annotation { "Feature Type Name" : "Feature", "Feature Type Description" : "" }
export const myFeature = defineFeature(function(context is Context, id is Id, definition is map)
    precondition{}
    {
        {
            var Q0;
            Q0=qCreatedBy(makeId("Right.planeOp"),FACE);
            var sketch = newSketch(context, id + "F0", { "sketchPlane" : qUnion([Q0])});
            skFitSpline(sketch, "E0", {"points": [v(-57.8, 46.93) * mm, v(-52.74, 44.85) * mm, v(-66.15, 19.52) * mm], "startDerivative": vector(22.12, -2.36) * mm, "endDerivative": vector(-31.77, -46.68) * mm});
            skFitSpline(sketch, "E1", {"points": [v(-66.15, 19.52) * mm, v(-70.33, 23.7) * mm], "startDerivative": vector(-4.17, 4.17) * mm, "endDerivative": vector(-4.17, 4.17) * mm});
            skFitSpline(sketch, "E2", {"points": [v(-70.33, 23.7) * mm, v(-55.57, 46.7) * mm], "startDerivative": vector(14.76, 23) * mm, "endDerivative": vector(14.76, 23) * mm});
            skSolve(sketch);
        }
        {
            var Q0;
            Q0=qCreatedBy(makeId("Right.planeOp"),FACE);
            var sketch = newSketch(context, id + "F1", { "sketchPlane" : qUnion([Q0])});
            skFitSpline(sketch, "E3", {"points": [v(-47.68, 42.46) * mm, v(-44.4, 40.68) * mm, v(-56.32, 17.13) * mm, v(-59.9, 19.52) * mm, v(-47.68, 42.46) * mm]});
            skFitSpline(sketch, "E4", {"points": [v(-39.33, 37.7) * mm, v(-35.16, 34.42) * mm, v(-45.6, 14.15) * mm, v(-49.17, 15.94) * mm, v(-39.33, 37.7) * mm]});
            skSolve(sketch);
        }
        {
            var Q0;
            Q0=qCreatedBy(makeId("Right.planeOp"),FACE);
            var sketch = newSketch(context, id + "F2", { "sketchPlane" : qUnion([Q0])});
            skText(sketch, "E5", { "text": "Adida\'s", "fontName": "OpenSans-Regular.ttf"});
            const initialGuessF2  = {"E5": [-0.0745, 0.00372, 1, 0, 0.00954]};
            skSetInitialGuess(sketch, initialGuessF2);
            skSolve(sketch);
        }
        {
            var Q0;
            Q0=qCreatedBy(makeId("Right.planeOp"),FACE);
            var sketch = newSketch(context, id + "F3", { "sketchPlane" : qUnion([Q0])});
            skFitSpline(sketch, "E6", {"points": [v(-63.77, -27.27) * mm, v(-61.98, -35.9) * mm, v(-13.7, -9.68) * mm, v(-13.11, -9.68) * mm], "startDerivative": vector(-9.49, -47.77) * mm, "endDerivative": vector(3.68, -3.66) * mm});
            skFitSpline(sketch, "E7", {"points": [v(-63.77, -27.27) * mm, v(-59.6, -31.44) * mm, v(-15.8, -7) * mm, v(-13.7, -7) * mm], "startDerivative": vector(8.17, -29.74) * mm, "endDerivative": vector(8.8, -5.9) * mm});
            skSolve(sketch);
        }
        {
            var Q0;
            Q0=qCreatedBy(makeId("Right.planeOp"),FACE);
            var sketch = newSketch(context, id + "F4", { "sketchPlane" : qUnion([Q0])});
            skText(sketch, "E8", { "text": "NIKE", "fontName": "OpenSans-Regular.ttf"});
            const initialGuessF4  = {"E8": [-0.06824, -0.05766, 1, 0, 0.01013]};
            skSetInitialGuess(sketch, initialGuessF4);
            skSolve(sketch);
        }
        {
            var Q0;
            Q0 = qSketchRegion(id + "F4", true);
            extrude(context, id + "F5", {"entities" : qUnion([Q0]), "depth" : 25.4 * mm, "offsetDistance" : 25.4 * mm});
        }
        {
            var Q0;
            Q0 = qSketchRegion(id + "F2", true);
            extrude(context, id + "F6", {"entities" : qUnion([Q0]), "depth" : 25.4 * mm, "offsetDistance" : 25.4 * mm});
        }
        {
            var Q0;
            Q0=qCreatedBy(makeId("Right.planeOp"),FACE);
            var sketch = newSketch(context, id + "F7", { "sketchPlane" : qUnion([Q0])});
            skText(sketch, "E9", { "text": "UNDER ARMOUR", "fontName": "OpenSans-Regular.ttf"});
            const initialGuessF7  = {"E9": [0.00447, 0.00372, 1, 0, 0.00894]};
            skSetInitialGuess(sketch, initialGuessF7);
            skSolve(sketch);
        }
        {
            var Q0;
            Q0 = qSketchRegion(id + "F7", true);
            extrude(context, id + "F8", {"entities" : qUnion([Q0]), "depth" : 25.4 * mm, "offsetDistance" : 25.4 * mm});
        }
        {
            var Q0;
            Q0=makeQuery(id+"F6.opExtrude","CAP_FACE",FACE,{"disambiguationData":[OSD([sQuery(id+"F2.wireOp",EDGE,"E5.sketch_text.stroke-73"),sQuery(id+"F2.wireOp",EDGE,"E5.sketch_text.stroke-74"),sQuery(id+"F2.wireOp",EDGE,"E5.sketch_text.stroke-75"),sQuery(id+"F2.wireOp",EDGE,"E5.sketch_text.stroke-76"),sQuery(id+"F2.wireOp",EDGE,"E5.sketch_text.stroke-77"),sQuery(id+"F2.wireOp",EDGE,"E5.sketch_text.stroke-78"),sQuery(id+"F2.wireOp",EDGE,"E5.sketch_text.stroke-79"),sQuery(id+"F2.wireOp",EDGE,"E5.sketch_text.stroke-80"),sQuery(id+"F2.wireOp",EDGE,"E5.sketch_text.stroke-81"),sQuery(id+"F2.wireOp",EDGE,"E5.sketch_text.stroke-82"),sQuery(id+"F2.wireOp",EDGE,"E5.sketch_text.stroke-83"),sQuery(id+"F2.wireOp",EDGE,"E5.sketch_text.stroke-84"),sQuery(id+"F2.wireOp",EDGE,"E5.sketch_text.stroke-85"),sQuery(id+"F2.wireOp",EDGE,"E5.sketch_text.stroke-86"),sQuery(id+"F2.wireOp",EDGE,"E5.sketch_text.stroke-87"),sQuery(id+"F2.wireOp",EDGE,"E5.sketch_text.stroke-88"),sQuery(id+"F2.wireOp",EDGE,"E5.sketch_text.stroke-89"),sQuery(id+"F2.wireOp",EDGE,"E5.sketch_text.stroke-90"),sQuery(id+"F2.wireOp",EDGE,"E5.sketch_text.stroke-91"),sQuery(id+"F2.wireOp",EDGE,"E5.sketch_text.stroke-92"),sQuery(id+"F2.wireOp",EDGE,"E5.sketch_text.stroke-93"),sQuery(id+"F2.wireOp",EDGE,"E5.sketch_text.stroke-94"),sQuery(id+"F2.wireOp",EDGE,"E5.sketch_text.stroke-95"),sQuery(id+"F2.wireOp",EDGE,"E5.sketch_text.stroke-96"),sQuery(id+"F2.wireOp",EDGE,"E5.sketch_text.stroke-97"),sQuery(id+"F2.wireOp",EDGE,"E5.sketch_text.stroke-98"),sQuery(id+"F2.wireOp",EDGE,"E5.sketch_text.stroke-99")])],"isStart":false});
            var sketch = newSketch(context, id + "F9", { "sketchPlane" : qUnion([Q0])});
            skText(sketch, "E10", { "text": "Reebok\n", "fontName": "OpenSans-Regular.ttf"});
            const initialGuessF9  = {"E10": [0.00547, -0.06362, 1, 0, 0.00954]};
            skSetInitialGuess(sketch, initialGuessF9);
            skSolve(sketch);
        }
        {
            var Q0;
            Q0 = qSketchRegion(id + "F9", true);
            extrude(context, id + "F10", {"entities" : qUnion([Q0]), "depth" : 25.4 * mm, "offsetDistance" : 25.4 * mm});
        }
        {
            var Q0;
            Q0=sQuery(id+"F3.wireOp",EDGE,"E7");
            var Q1;
            Q1=sQuery(id+"F3.wireOp",EDGE,"E6");
            extrude(context, id + "F11", {"bodyType" : ToolBodyType.SURFACE, "surfaceEntities" : qUnion([Q0, Q1]), "depth" : 25.4 * mm, "offsetDistance" : 25.4 * mm});
        }
        {
            var Q0;
            {var subQ0=sQuery(id+"F0.wireOp",EDGE,"E1");Q0=makeQuery(id+"F0.imprint","IMPRINT",FACE,{"disambiguationData":[TD([[makeQuery(id+"F0.imprint","IMPRINT",EDGE,{"derivedFrom":subQ0}),-1.0]])]});}
            extrude(context, id + "F12", {"entities" : qUnion([Q0]), "depth" : 25.4 * mm, "offsetDistance" : 25.4 * mm});
        }
        {
            var Q0;
            Q0=makeQuery(id+"F1.imprint","IMPRINT",FACE,{"disambiguationData":[TD([[makeQuery(id+"F1.imprint","IMPRINT",EDGE,{"derivedFrom":sQuery(id+"F1.wireOp",EDGE,"E3")}),-1.0]])]});
            var Q1;
            Q1=makeQuery(id+"F1.imprint","IMPRINT",FACE,{"disambiguationData":[TD([[makeQuery(id+"F1.imprint","IMPRINT",EDGE,{"derivedFrom":sQuery(id+"F1.wireOp",EDGE,"E4")}),-1.0]])]});
            extrude(context, id + "F13", {"entities" : qUnion([Q0, Q1]), "operationType" : NewBodyOperationType.ADD, "depth" : 25.4 * mm, "offsetDistance" : 25.4 * mm});
        }
    });